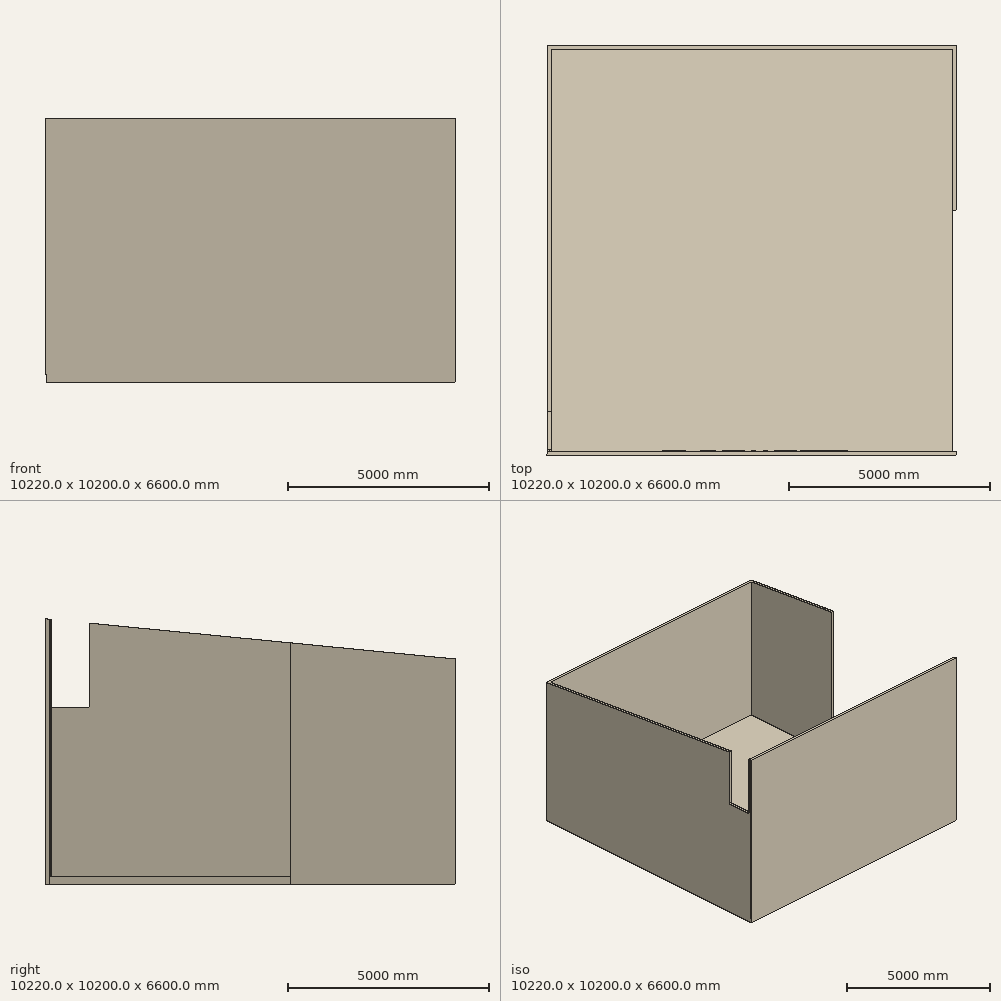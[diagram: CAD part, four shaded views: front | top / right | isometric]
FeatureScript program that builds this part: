
annotation { "Feature Type Name" : "Feature", "Feature Type Description" : "" }
export const myFeature = defineFeature(function(context is Context, id is Id, definition is map)
    precondition{}
    {
        {
            var Q0;
            Q0=qCreatedBy(makeId("Top.planeOp"),FACE);
            var sketch = newSketch(context, id + "F0", { "sketchPlane" : qUnion([Q0])});
            skLineSegment(sketch, "E0.bottom", {"start": v(0, 0) * mm, "end": v(10000, 0) * mm});
            skLineSegment(sketch, "E0.top", {"start": v(0, 10000) * mm, "end": v(10000, 10000) * mm});
            skLineSegment(sketch, "E0.left", {"start": v(0, 0) * mm, "end": v(0, 10000) * mm});
            skLineSegment(sketch, "E0.right", {"start": v(10000, 0) * mm, "end": v(10000, 10000) * mm});
            skLineSegment(sketch, "E1.0", {"start": v(10100, -100) * mm, "end": v(10100, 10100) * mm});
            skLineSegment(sketch, "E1.1", {"start": v(-100, -100) * mm, "end": v(10100, -100) * mm});
            skLineSegment(sketch, "E1.2", {"start": v(-100, -100) * mm, "end": v(-100, 10100) * mm});
            skLineSegment(sketch, "E1.3", {"start": v(-100, 10100) * mm, "end": v(10100, 10100) * mm});
            skSolve(sketch);
        }
        {
            var Q0;
            Q0 = qSketchRegion(id + "F0", true);
            var Q1;
            Q1=makeQuery(id+"F0.imprint","IMPRINT",FACE,{"disambiguationData":[TD([[makeQuery(id+"F0.imprint","IMPRINT",EDGE,{"derivedFrom":sQuery(id+"F0.wireOp",EDGE,"NNFDGGjW-2WEX-GjtB-ggQC-qw6gqxpLpsvo")}),-1.0]])]});
            extrude(context, id + "F1", {"entities" : qUnion([Q0, Q1]), "depth" : 25 * mm});
        }
        {
            var Q0;
            Q0 = qSketchRegion(id + "F0", true);
            extrude(context, id + "F2", {"entities" : qUnion([Q0]), "operationType" : NewBodyOperationType.ADD, "depth" : 6750 * mm});
        }
        {
            var Q0;
            {var subQ0=sQuery(id+"F0.wireOp",EDGE,"E1.1");Q0=makeQuery(id+"F2.boolean.opBoolean","MERGE",FACE,{"derivedFrom":[makeQuery(id+"F1.opExtrude","SWEPT_FACE",FACE,{"disambiguationData":[OSD([subQ0])]}),makeQuery(id+"F2.opExtrude","SWEPT_FACE",FACE,{"disambiguationData":[OSD([subQ0])]})]});}
            var sketch = newSketch(context, id + "F3", { "sketchPlane" : qUnion([Q0])});
            skLineSegment(sketch, "E2.bottom", {"start": v(-100, 0) * mm, "end": v(10100, 0) * mm});
            skLineSegment(sketch, "E2.top", {"start": v(-100, -200) * mm, "end": v(10100, -200) * mm});
            skLineSegment(sketch, "E2.left", {"start": v(-100, -200) * mm, "end": v(-100, 0) * mm});
            skLineSegment(sketch, "E2.right", {"start": v(10100, -200) * mm, "end": v(10100, 0) * mm});
            skSolve(sketch);
        }
        {
            var Q0;
            Q0 = qSketchRegion(id + "F3", true);
            var Q1;
            {var subQ0=sQuery(id+"F0.wireOp",EDGE,"E1.3");Q1=makeQuery(id+"F2.boolean.opBoolean","MERGE",FACE,{"derivedFrom":[makeQuery(id+"F1.opExtrude","SWEPT_FACE",FACE,{"disambiguationData":[OSD([subQ0])]}),makeQuery(id+"F2.opExtrude","SWEPT_FACE",FACE,{"disambiguationData":[OSD([subQ0])]})]});}
            extrude(context, id + "F4", {"entities" : qUnion([Q0]), "operationType" : NewBodyOperationType.ADD, "endBound" : BoundingType.UP_TO_SURFACE, "oppositeDirection" : true, "endBoundEntityFace" : qUnion([Q1]), "depth" : 25 * mm});
        }
        {
            var Q0;
            {var subQ0=sQuery(id+"F0.wireOp",EDGE,"E1.0");Q0=makeQuery(id+"F4.boolean.opBoolean","MERGE",FACE,{"derivedFrom":[makeQuery(id+"F2.boolean.opBoolean","MERGE",FACE,{"derivedFrom":[makeQuery(id+"F1.opExtrude","SWEPT_FACE",FACE,{"disambiguationData":[OSD([subQ0])]}),makeQuery(id+"F2.opExtrude","SWEPT_FACE",FACE,{"disambiguationData":[OSD([subQ0])]})]}),makeQuery(id+"F4.opExtrude","SWEPT_FACE",FACE,{"disambiguationData":[OSD([sQuery(id+"F3.wireOp",EDGE,"E2.right")])]})]});}
            var sketch = newSketch(context, id + "F5", { "sketchPlane" : qUnion([Q0])});
            skLineSegment(sketch, "E3", {"start": v(10100, 5400) * mm, "end": v(-100, 6400) * mm});
            skLineSegment(sketch, "E4", {"start": v(-100, 6400) * mm, "end": v(-100, 6903.08) * mm});
            skLineSegment(sketch, "E5", {"start": v(-100, 6903.08) * mm, "end": v(10100, 6903.08) * mm});
            skLineSegment(sketch, "E6", {"start": v(10100, 6903.08) * mm, "end": v(10100, 5400) * mm});
            skSolve(sketch);
        }
        {
            var Q0;
            Q0 = qSketchRegion(id + "F5", true);
            extrude(context, id + "F6", {"entities" : qUnion([Q0]), "operationType" : NewBodyOperationType.REMOVE, "endBound" : BoundingType.THROUGH_ALL, "oppositeDirection" : true, "depth" : 25 * mm});
        }
        {
            var Q0;
            {var subQ0=sQuery(id+"F0.wireOp",EDGE,"E0.left");Q0=makeQuery(id+"F2.boolean.opBoolean","MERGE",FACE,{"derivedFrom":[makeQuery(id+"F1.opExtrude","SWEPT_FACE",FACE,{"disambiguationData":[OSD([subQ0])]}),makeQuery(id+"F2.opExtrude","SWEPT_FACE",FACE,{"disambiguationData":[OSD([subQ0])]})]});}
            var sketch = newSketch(context, id + "F7", { "sketchPlane" : qUnion([Q0])});
            skLineSegment(sketch, "E7.bottom", {"start": v(0, 6390.2) * mm, "end": v(1000, 6390.2) * mm});
            skLineSegment(sketch, "E7.top", {"start": v(0, 4190.2) * mm, "end": v(1000, 4190.2) * mm});
            skLineSegment(sketch, "E7.left", {"start": v(0, 6390.2) * mm, "end": v(0, 4190.2) * mm});
            skLineSegment(sketch, "E7.right", {"start": v(1000, 6390.2) * mm, "end": v(1000, 4190.2) * mm});
            skSolve(sketch);
        }
        {
            var Q0;
            Q0 = qSketchRegion(id + "F7", true);
            var Q1;
            {var subQ0=sQuery(id+"F0.wireOp",EDGE,"E1.0");Q1=makeQuery(id+"F4.boolean.opBoolean","MERGE",FACE,{"derivedFrom":[makeQuery(id+"F2.boolean.opBoolean","MERGE",FACE,{"derivedFrom":[makeQuery(id+"F1.opExtrude","SWEPT_FACE",FACE,{"disambiguationData":[OSD([subQ0])]}),makeQuery(id+"F2.opExtrude","SWEPT_FACE",FACE,{"disambiguationData":[OSD([subQ0])]})]}),makeQuery(id+"F4.opExtrude","SWEPT_FACE",FACE,{"disambiguationData":[OSD([sQuery(id+"F3.wireOp",EDGE,"E2.right")])]})]});}
            extrude(context, id + "F8", {"entities" : qUnion([Q0]), "operationType" : NewBodyOperationType.REMOVE, "oppositeDirection" : true, "depth" : 1400 * mm, "hasSecondDirection" : true, "secondDirectionOppositeDirection" : false, "secondDirectionBoundEntityFace" : qUnion([Q1]), "secondDirectionDepth" : 11390 * mm});
        }
        {
            var Q0;
            {var subQ0=sQuery(id+"F0.wireOp",EDGE,"E1.0");Q0=makeQuery(id+"F4.boolean.opBoolean","MERGE",FACE,{"derivedFrom":[makeQuery(id+"F2.boolean.opBoolean","MERGE",FACE,{"derivedFrom":[makeQuery(id+"F1.opExtrude","SWEPT_FACE",FACE,{"disambiguationData":[OSD([subQ0])]}),makeQuery(id+"F2.opExtrude","SWEPT_FACE",FACE,{"disambiguationData":[OSD([subQ0])]})]}),makeQuery(id+"F4.opExtrude","SWEPT_FACE",FACE,{"disambiguationData":[OSD([sQuery(id+"F3.wireOp",EDGE,"E2.right")])]})]});}
            var sketch = newSketch(context, id + "F9", { "sketchPlane" : qUnion([Q0])});
            skLineSegment(sketch, "E8.bottom", {"start": v(0, 6390.2) * mm, "end": v(6000, 6390.2) * mm});
            skLineSegment(sketch, "E8.top", {"start": v(0, -200) * mm, "end": v(6000, -200) * mm});
            skLineSegment(sketch, "E8.left", {"start": v(0, 6390.2) * mm, "end": v(0, -200) * mm});
            skLineSegment(sketch, "E8.right", {"start": v(6000, 6390.2) * mm, "end": v(6000, -200) * mm});
            skSolve(sketch);
        }
        {
            var Q0;
            Q0 = qSketchRegion(id + "F9", true);
            var Q1;
            {var subQ0=sQuery(id+"F0.wireOp",EDGE,"E0.right");Q1=makeQuery(id+"F2.boolean.opBoolean","MERGE",FACE,{"derivedFrom":[makeQuery(id+"F1.opExtrude","SWEPT_FACE",FACE,{"disambiguationData":[OSD([subQ0])]}),makeQuery(id+"F2.opExtrude","SWEPT_FACE",FACE,{"disambiguationData":[OSD([subQ0])]})]});}
            extrude(context, id + "F10", {"entities" : qUnion([Q0]), "operationType" : NewBodyOperationType.REMOVE, "endBound" : BoundingType.UP_TO_SURFACE, "oppositeDirection" : true, "endBoundEntityFace" : qUnion([Q1]), "depth" : 25 * mm});
        }
        {
            var Q0;
            {var subQ0=sQuery(id+"F0.wireOp",EDGE,"E0.bottom");Q0=makeQuery(id+"F10.boolean.opBoolean","MERGE",FACE,{"derivedFrom":[makeQuery(id+"F8.boolean.opBoolean","MERGE",FACE,{"derivedFrom":[makeQuery(id+"F2.boolean.opBoolean","MERGE",FACE,{"derivedFrom":[makeQuery(id+"F1.opExtrude","SWEPT_FACE",FACE,{"disambiguationData":[OSD([subQ0])]}),makeQuery(id+"F2.opExtrude","SWEPT_FACE",FACE,{"disambiguationData":[OSD([subQ0])]})]})],"fromTools":[makeQuery(id+"F8.opExtrude","SWEPT_FACE",FACE,{"disambiguationData":[OSD([sQuery(id+"F7.wireOp",EDGE,"E7.left")])]})]})],"fromTools":[makeQuery(id+"F10.opExtrude","SWEPT_FACE",FACE,{"disambiguationData":[OSD([sQuery(id+"F9.wireOp",EDGE,"E8.left")])]})]});}
            var sketch = newSketch(context, id + "F11", { "sketchPlane" : qUnion([Q0])});
            skText(sketch, "E9", { "text": "Atelier 2", "fontName": "OpenSans-Regular.ttf"});
            const initialGuessF11  = {"E9": [-7.38633, 1.67127, 1, 0, 0.87602]};
            skSetInitialGuess(sketch, initialGuessF11);
            skSolve(sketch);
        }
        {
            var Q0;
            Q0 = qSketchRegion(id + "F11", true);
            extrude(context, id + "F12", {"entities" : qUnion([Q0]), "operationType" : NewBodyOperationType.ADD, "depth" : 25 * mm});
        }
        {
            var Q0;
            Q0=makeQuery(id+"F4.opExtrude","SWEPT_FACE",FACE,{"disambiguationData":[OSD([sQuery(id+"F3.wireOp",EDGE,"E2.bottom")])]});
            var sketch = newSketch(context, id + "F13", { "sketchPlane" : qUnion([Q0])});
            skLineSegment(sketch, "E10.1.0.0", {"start": v(-120, 40) * mm, "end": v(-50, 40) * mm});
            skLineSegment(sketch, "E10.1.0.1", {"start": v(-120, 30) * mm, "end": v(-120, 40) * mm});
            skLineSegment(sketch, "E10.1.0.2", {"start": v(-55, 30) * mm, "end": v(-120, 30) * mm});
            skLineSegment(sketch, "E10.1.0.3", {"start": v(-55, -90) * mm, "end": v(-55, 30) * mm});
            skLineSegment(sketch, "E10.1.0.4", {"start": v(-120, -90) * mm, "end": v(-55, -90) * mm});
            skLineSegment(sketch, "E10.1.0.5", {"start": v(-120, -100) * mm, "end": v(-120, -90) * mm});
            skLineSegment(sketch, "E10.1.0.6", {"start": v(-50, -100) * mm, "end": v(-120, -100) * mm});
            skLineSegment(sketch, "E10.1.0.7", {"start": v(-50, -100) * mm, "end": v(20, -100) * mm});
            skLineSegment(sketch, "E10.1.0.8", {"start": v(20, -100) * mm, "end": v(20, -90) * mm});
            skLineSegment(sketch, "E10.1.0.9", {"start": v(20, -90) * mm, "end": v(-45, -90) * mm});
            skLineSegment(sketch, "E10.1.0.10", {"start": v(-45, -90) * mm, "end": v(-45, 30) * mm});
            skLineSegment(sketch, "E10.1.0.11", {"start": v(-45, 30) * mm, "end": v(20, 30) * mm});
            skLineSegment(sketch, "E10.1.0.12", {"start": v(20, 30) * mm, "end": v(20, 40) * mm});
            skLineSegment(sketch, "E10.1.0.13", {"start": v(20, 40) * mm, "end": v(-50, 40) * mm});
            skLineSegment(sketch, "E11", {"start": v(-50, -100) * mm, "end": v(-50, 40) * mm, "construction": true});
            skLineSegment(sketch, "E12", {"start": v(0, 0) * mm, "end": v(-100, 0) * mm, "construction": true});
            skPoint(sketch, "E13", {"position": v(-50, 0) * mm});
            skSolve(sketch);
        }
        {
            var Q0;
            Q0 = qSketchRegion(id + "F13", true);
            var Q1;
            {var subQ4=sQuery(id+"F0.wireOp",EDGE,"E0.bottom");Q1=makeQuery(id+"F8.boolean.opBoolean","SPLIT",FACE,{"disambiguationData":[TD([makeQuery(id+"F1.opExtrude","SWEPT_FACE",FACE,{"disambiguationData":[OSD([subQ4])]})])],"derivedFrom":makeQuery(id+"F6.boolean.opBoolean","COPY",FACE,{"derivedFrom":makeQuery(id+"F6.opExtrude","SWEPT_FACE",FACE,{"disambiguationData":[OSD([sQuery(id+"F5.wireOp",EDGE,"E3")])]})})});}
            extrude(context, id + "F14", {"entities" : qUnion([Q0]), "operationType" : NewBodyOperationType.ADD, "endBound" : BoundingType.UP_TO_SURFACE, "endBoundEntityFace" : qUnion([Q1]), "depth" : 25 * mm});
        }
    });
